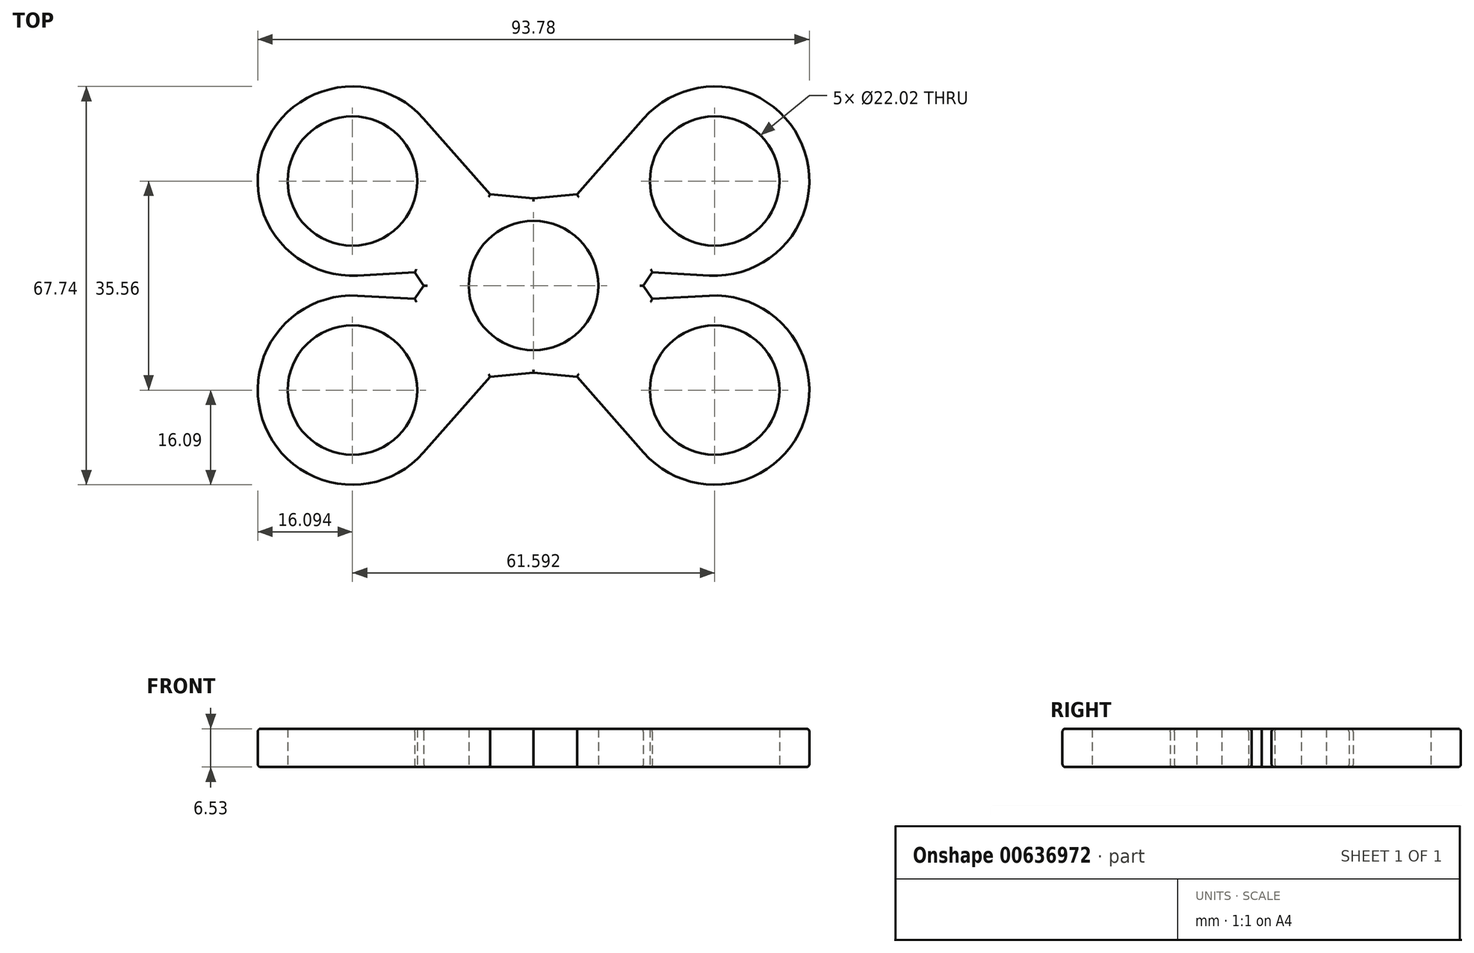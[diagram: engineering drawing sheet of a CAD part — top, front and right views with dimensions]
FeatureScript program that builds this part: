
annotation { "Feature Type Name" : "Feature", "Feature Type Description" : "" }
export const myFeature = defineFeature(function(context is Context, id is Id, definition is map)
    precondition{}
    {
        {
            var Q0;
            Q0=qCreatedBy(makeId("Top.planeOp"),FACE);
            var sketch = newSketch(context, id + "F0", { "sketchPlane" : qUnion([Q0])});
            skCircle(sketch, "E0", {"center": v(0, 0) * mm, "radius": 11.01 * mm});
            skLineSegment(sketch, "E1", {"start": v(18.66, 0) * mm, "end": v(20.2, 2.24) * mm});
            skLineSegment(sketch, "E2", {"start": v(-18.66, 0) * mm, "end": v(-20.2, -2.24) * mm});
            skLineSegment(sketch, "E3", {"start": v(-18.66, 0) * mm, "end": v(-20.2, 2.24) * mm});
            skLineSegment(sketch, "E4", {"start": v(18.66, 0) * mm, "end": v(20.2, -2.24) * mm});
            skCircle(sketch, "E5", {"center": v(30.8, 17.78) * mm, "radius": 11.01 * mm});
            skCircle(sketch, "E6", {"center": v(30.8, -17.78) * mm, "radius": 11.01 * mm});
            skCircle(sketch, "E7", {"center": v(-30.8, -17.78) * mm, "radius": 11.01 * mm});
            skCircle(sketch, "E8", {"center": v(-30.8, 17.78) * mm, "radius": 11.01 * mm});
            skArc(sketch, "E9", {"start": v(29.92, 1.71) * mm, "mid": v(45.63, 24) * mm, "end": v(18.72, 28.42) * mm});
            skArc(sketch, "E10", {"start": v(18.72, -28.42) * mm, "mid": v(45.63, -24) * mm, "end": v(29.92, -1.71) * mm});
            skArc(sketch, "E11", {"start": v(-29.92, -1.71) * mm, "mid": v(-45.63, -24) * mm, "end": v(-18.72, -28.42) * mm});
            skArc(sketch, "E12", {"start": v(-18.72, 28.42) * mm, "mid": v(-45.63, 24) * mm, "end": v(-29.92, 1.71) * mm});
            skLineSegment(sketch, "E13", {"start": v(0, 14.85) * mm, "end": v(7.39, 15.55) * mm});
            skLineSegment(sketch, "E14", {"start": v(0, -14.85) * mm, "end": v(7.39, -15.55) * mm});
            skLineSegment(sketch, "E15", {"start": v(0, -14.85) * mm, "end": v(-7.39, -15.55) * mm});
            skLineSegment(sketch, "E16", {"start": v(0, 14.85) * mm, "end": v(-7.39, 15.55) * mm});
            skLineSegment(sketch, "E17", {"start": v(20.2, 2.24) * mm, "end": v(29.92, 1.71) * mm});
            skLineSegment(sketch, "E18", {"start": v(7.39, 15.55) * mm, "end": v(18.72, 28.42) * mm});
            skLineSegment(sketch, "E19", {"start": v(7.39, -15.55) * mm, "end": v(18.72, -28.42) * mm});
            skLineSegment(sketch, "E20", {"start": v(20.2, -2.24) * mm, "end": v(29.92, -1.71) * mm});
            skLineSegment(sketch, "E21", {"start": v(-7.39, -15.55) * mm, "end": v(-18.72, -28.42) * mm});
            skLineSegment(sketch, "E22", {"start": v(-20.2, -2.24) * mm, "end": v(-29.92, -1.71) * mm});
            skLineSegment(sketch, "E23", {"start": v(-20.2, 2.24) * mm, "end": v(-29.92, 1.71) * mm});
            skLineSegment(sketch, "E24", {"start": v(-7.39, 15.55) * mm, "end": v(-18.72, 28.42) * mm});
            skPoint(sketch, "E25.orphan", {"position": v(14.78, 16.25) * mm});
            skPoint(sketch, "E26.orphan", {"position": v(21.73, 4.49) * mm});
            skPoint(sketch, "E27.orphan", {"position": v(21.73, -4.49) * mm});
            skPoint(sketch, "E28.orphan", {"position": v(14.78, -16.25) * mm});
            skPoint(sketch, "E29.orphan", {"position": v(-14.78, -16.25) * mm});
            skPoint(sketch, "E30.orphan", {"position": v(-21.73, -4.49) * mm});
            skPoint(sketch, "E31.orphan", {"position": v(-21.73, 4.49) * mm});
            skPoint(sketch, "E32.orphan", {"position": v(-14.78, 16.25) * mm});
            skLineSegment(sketch, "E33", {"start": v(-30.8, 17.78) * mm, "end": v(0, 0) * mm});
            skLineSegment(sketch, "E34", {"start": v(-30.8, -17.78) * mm, "end": v(0, 0) * mm});
            skLineSegment(sketch, "E35", {"start": v(0, 0) * mm, "end": v(30.8, 17.78) * mm});
            skLineSegment(sketch, "E36", {"start": v(0, 0) * mm, "end": v(30.8, -17.78) * mm});
            skLineSegment(sketch, "E37", {"start": v(0, 14.85) * mm, "end": v(0, -14.85) * mm});
            skLineSegment(sketch, "E38", {"start": v(-18.66, 0) * mm, "end": v(18.66, 0) * mm});
            skLineSegment(sketch, "E39", {"start": v(-20.2, 2.24) * mm, "end": v(0, 0) * mm});
            skLineSegment(sketch, "E40", {"start": v(-20.2, -2.24) * mm, "end": v(0, 0) * mm});
            skLineSegment(sketch, "E41", {"start": v(0, 0) * mm, "end": v(20.2, -2.24) * mm});
            skLineSegment(sketch, "E42", {"start": v(20.2, 2.24) * mm, "end": v(0, 0) * mm});
            skSolve(sketch);
        }
        {
            var Q0;
            Q0=makeQuery(id+"F0.imprint","IMPRINT",FACE,{"disambiguationData":[TD([[makeQuery(id+"F0.imprint","IMPRINT",EDGE,{"derivedFrom":sQuery(id+"F0.wireOp",EDGE,"E0")}),-1.0]])]});
            var Q1;
            {var subQ5=sQuery(id+"F0.wireOp",EDGE,"E3");Q1=makeQuery(id+"F0.imprint","IMPRINT",FACE,{"disambiguationData":[TD([[makeQuery(id+"F0.imprint","IMPRINT",EDGE,{"derivedFrom":subQ5}),-1.0]])]});}
            var Q2;
            {var subQ5=sQuery(id+"F0.wireOp",EDGE,"E2");Q2=makeQuery(id+"F0.imprint","IMPRINT",FACE,{"disambiguationData":[TD([[makeQuery(id+"F0.imprint","IMPRINT",EDGE,{"derivedFrom":subQ5}),1.0]])]});}
            var Q3;
            {var subQ5=sQuery(id+"F0.wireOp",EDGE,"E1");Q3=makeQuery(id+"F0.imprint","IMPRINT",FACE,{"disambiguationData":[TD([[makeQuery(id+"F0.imprint","IMPRINT",EDGE,{"derivedFrom":subQ5}),1.0]])]});}
            var Q4;
            {var subQ5=sQuery(id+"F0.wireOp",EDGE,"E4");Q4=makeQuery(id+"F0.imprint","IMPRINT",FACE,{"disambiguationData":[TD([[makeQuery(id+"F0.imprint","IMPRINT",EDGE,{"derivedFrom":subQ5}),-1.0]])]});}
            extrude(context, id + "F1", {"entities" : qUnion([Q0, Q1, Q2, Q3, Q4]), "depth" : 6.53 * mm, "offsetDistance" : 25.4 * mm});
        }
        {
            var Q0;
            Q0=makeQuery(id+"F1.opExtrude","CAP_EDGE",EDGE,{"disambiguationData":[OSD([sQuery(id+"F0.wireOp",EDGE,"E12")])],"isStart":false});
            var Q1;
            Q1=makeQuery(id+"F1.opExtrude","CAP_EDGE",EDGE,{"disambiguationData":[OSD([sQuery(id+"F0.wireOp",EDGE,"E16")])],"isStart":false});
            var Q2;
            Q2=makeQuery(id+"F1.opExtrude","CAP_EDGE",EDGE,{"disambiguationData":[OSD([sQuery(id+"F0.wireOp",EDGE,"E13")])],"isStart":false});
            var Q3;
            Q3=makeQuery(id+"F1.opExtrude","CAP_EDGE",EDGE,{"disambiguationData":[OSD([sQuery(id+"F0.wireOp",EDGE,"E9")])],"isStart":false});
            var Q4;
            Q4=makeQuery(id+"F1.opExtrude","CAP_EDGE",EDGE,{"disambiguationData":[OSD([sQuery(id+"F0.wireOp",EDGE,"E1")])],"isStart":false});
            var Q5;
            Q5=makeQuery(id+"F1.opExtrude","CAP_EDGE",EDGE,{"disambiguationData":[OSD([sQuery(id+"F0.wireOp",EDGE,"E4")])],"isStart":false});
            var Q6;
            Q6=makeQuery(id+"F1.opExtrude","CAP_EDGE",EDGE,{"disambiguationData":[OSD([sQuery(id+"F0.wireOp",EDGE,"E10")])],"isStart":false});
            var Q7;
            Q7=makeQuery(id+"F1.opExtrude","CAP_EDGE",EDGE,{"disambiguationData":[OSD([sQuery(id+"F0.wireOp",EDGE,"E14")])],"isStart":false});
            var Q8;
            Q8=makeQuery(id+"F1.opExtrude","CAP_EDGE",EDGE,{"disambiguationData":[OSD([sQuery(id+"F0.wireOp",EDGE,"E15")])],"isStart":false});
            var Q9;
            Q9=makeQuery(id+"F1.opExtrude","CAP_EDGE",EDGE,{"disambiguationData":[OSD([sQuery(id+"F0.wireOp",EDGE,"E11")])],"isStart":false});
            var Q10;
            Q10=makeQuery(id+"F1.opExtrude","CAP_EDGE",EDGE,{"disambiguationData":[OSD([sQuery(id+"F0.wireOp",EDGE,"E2")])],"isStart":false});
            var Q11;
            Q11=makeQuery(id+"F1.opExtrude","CAP_EDGE",EDGE,{"disambiguationData":[OSD([sQuery(id+"F0.wireOp",EDGE,"E3")])],"isStart":false});
            var Q12;
            Q12=makeQuery(id+"F1.opExtrude","CAP_EDGE",EDGE,{"disambiguationData":[OSD([sQuery(id+"F0.wireOp",EDGE,"E9")])],"isStart":true});
            var Q13;
            Q13=makeQuery(id+"F1.opExtrude","CAP_EDGE",EDGE,{"disambiguationData":[OSD([sQuery(id+"F0.wireOp",EDGE,"E13")])],"isStart":true});
            var Q14;
            Q14=makeQuery(id+"F1.opExtrude","CAP_EDGE",EDGE,{"disambiguationData":[OSD([sQuery(id+"F0.wireOp",EDGE,"E16")])],"isStart":true});
            var Q15;
            Q15=makeQuery(id+"F1.opExtrude","CAP_EDGE",EDGE,{"disambiguationData":[OSD([sQuery(id+"F0.wireOp",EDGE,"E12")])],"isStart":true});
            var Q16;
            Q16=makeQuery(id+"F1.opExtrude","CAP_EDGE",EDGE,{"disambiguationData":[OSD([sQuery(id+"F0.wireOp",EDGE,"E3")])],"isStart":true});
            var Q17;
            Q17=makeQuery(id+"F1.opExtrude","CAP_EDGE",EDGE,{"disambiguationData":[OSD([sQuery(id+"F0.wireOp",EDGE,"E2")])],"isStart":true});
            var Q18;
            Q18=makeQuery(id+"F1.opExtrude","CAP_EDGE",EDGE,{"disambiguationData":[OSD([sQuery(id+"F0.wireOp",EDGE,"E11")])],"isStart":true});
            var Q19;
            Q19=makeQuery(id+"F1.opExtrude","CAP_EDGE",EDGE,{"disambiguationData":[OSD([sQuery(id+"F0.wireOp",EDGE,"E15")])],"isStart":true});
            var Q20;
            Q20=makeQuery(id+"F1.opExtrude","CAP_EDGE",EDGE,{"disambiguationData":[OSD([sQuery(id+"F0.wireOp",EDGE,"E14")])],"isStart":true});
            var Q21;
            Q21=makeQuery(id+"F1.opExtrude","CAP_EDGE",EDGE,{"disambiguationData":[OSD([sQuery(id+"F0.wireOp",EDGE,"E10")])],"isStart":true});
            var Q22;
            Q22=makeQuery(id+"F1.opExtrude","CAP_EDGE",EDGE,{"disambiguationData":[OSD([sQuery(id+"F0.wireOp",EDGE,"E4")])],"isStart":true});
            var Q23;
            Q23=makeQuery(id+"F1.opExtrude","CAP_EDGE",EDGE,{"disambiguationData":[OSD([sQuery(id+"F0.wireOp",EDGE,"E1")])],"isStart":true});
            var Q24;
            Q24=makeQuery(id+"F1.opExtrude","CAP_EDGE",EDGE,{"disambiguationData":[OSD([sQuery(id+"F0.wireOp",EDGE,"E24")])],"isStart":false});
            var Q25;
            Q25=makeQuery(id+"F1.opExtrude","CAP_EDGE",EDGE,{"disambiguationData":[OSD([sQuery(id+"F0.wireOp",EDGE,"E18")])],"isStart":false});
            var Q26;
            Q26=makeQuery(id+"F1.opExtrude","CAP_EDGE",EDGE,{"disambiguationData":[OSD([sQuery(id+"F0.wireOp",EDGE,"E17")])],"isStart":false});
            var Q27;
            Q27=makeQuery(id+"F1.opExtrude","CAP_EDGE",EDGE,{"disambiguationData":[OSD([sQuery(id+"F0.wireOp",EDGE,"E20")])],"isStart":false});
            var Q28;
            Q28=makeQuery(id+"F1.opExtrude","CAP_EDGE",EDGE,{"disambiguationData":[OSD([sQuery(id+"F0.wireOp",EDGE,"E19")])],"isStart":false});
            var Q29;
            Q29=makeQuery(id+"F1.opExtrude","CAP_EDGE",EDGE,{"disambiguationData":[OSD([sQuery(id+"F0.wireOp",EDGE,"E21")])],"isStart":false});
            var Q30;
            Q30=makeQuery(id+"F1.opExtrude","CAP_EDGE",EDGE,{"disambiguationData":[OSD([sQuery(id+"F0.wireOp",EDGE,"E22")])],"isStart":false});
            var Q31;
            Q31=makeQuery(id+"F1.opExtrude","CAP_EDGE",EDGE,{"disambiguationData":[OSD([sQuery(id+"F0.wireOp",EDGE,"E23")])],"isStart":false});
            var Q32;
            Q32=makeQuery(id+"F1.opExtrude","CAP_EDGE",EDGE,{"disambiguationData":[OSD([sQuery(id+"F0.wireOp",EDGE,"E24")])],"isStart":true});
            var Q33;
            Q33=makeQuery(id+"F1.opExtrude","CAP_EDGE",EDGE,{"disambiguationData":[OSD([sQuery(id+"F0.wireOp",EDGE,"E18")])],"isStart":true});
            var Q34;
            Q34=makeQuery(id+"F1.opExtrude","CAP_EDGE",EDGE,{"disambiguationData":[OSD([sQuery(id+"F0.wireOp",EDGE,"E21")])],"isStart":true});
            var Q35;
            Q35=makeQuery(id+"F1.opExtrude","CAP_EDGE",EDGE,{"disambiguationData":[OSD([sQuery(id+"F0.wireOp",EDGE,"E19")])],"isStart":true});
            fillet(context, id + "F2", {"entities" : qUnion([Q0, Q1, Q2, Q3, Q4, Q5, Q6, Q7, Q8, Q9, Q10, Q11, Q12, Q13, Q14, Q15, Q16, Q17, Q18, Q19, Q20, Q21, Q22, Q23, Q24, Q25, Q26, Q27, Q28, Q29, Q30, Q31, Q32, Q33, Q34, Q35]), "radius" : 0.5 * mm, "tangentPropagation" : true, "allowEdgeOverflow" : false});
        }
    });
